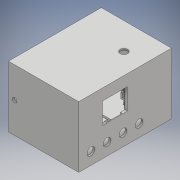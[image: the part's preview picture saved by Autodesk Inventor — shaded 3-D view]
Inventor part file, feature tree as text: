
AUTODESK INVENTOR PART (.ipt)
format: ipt  version: 2018 (Build 220112000, 112)  size: 893,952 bytes
history: native  units: mm
features: sketch x52, extrude x51, other x7
ambient origin geometry x8: Origin, YZ Plane, XZ Plane, XY Plane, X Axis, Y Axis, Z Axis, Center Point
bodies: Body1 (feature_tree)
feature tree (110):
  other  "Sólido1"
  extrude  "Extrusão1"  Depth=156.0mm
  extrude  "Extrusão2"  Depth=3.0mm
  extrude  "Extrusão3"  Depth=3.0mm
  extrude  "Extrusão4"  Depth=100.0mm TaperAngle=0.0deg
  extrude  "Extrusão6"  Depth=5.0mm
  extrude  "Extrusão8"  Depth=5.0mm
  extrude  "Extrusão9"  Depth=70.0mm
  other  "Plano de trabalho3"
  extrude  "Extrusão14"  Depth=7.0mm TaperAngle=0.0deg
  sketch  "Esboço32"  dims[d50=12.0mm d52=12.0mm]
  other  "Plano de trabalho4"
  extrude  "Extrusão15"  Depth=12.0mm
  extrude  "Extrusão16"  Depth=12.0mm
  other  "Plano de trabalho8"
  other  "Plano de trabalho9"
  extrude  "Extrusão19"  Depth=27.0mm
  extrude  "Extrusão20"  Depth=27.0mm
  extrude  "Extrusão21"  Depth=40.5mm
  extrude  "Extrusão22"  Depth=28.5mm
  other  "Plano de trabalho10"
  extrude  "Extrusão27"  Depth=28.5mm
  extrude  "Extrusão28"  Depth=20.5mm
  extrude  "Extrusão31"  Depth=20.25mm TaperAngle=0.0deg
  extrude  "Extrusão32"  Depth=5.25mm
  extrude  "Extrusão33"  Depth=52.0mm
  extrude  "Extrusão34"  Depth=3.0mm
  extrude  "Extrusão35"  Depth=3.0mm
  other  "Plano de trabalho11"
  extrude  "Extrusão36"  Depth=1.25mm
  extrude  "Extrusão37"  Depth=5.25mm
  extrude  "Extrusão38"  Depth=1.0mm
  extrude  "Extrusão39"  Depth=7.0mm
  extrude  "Extrusão40"  Depth=1.0mm
  extrude  "Extrusão41"  Depth=5.0mm
  extrude  "Extrusão42"  Depth=3.0mm TaperAngle=0.0deg
  extrude  "Extrusão43"  Depth=51.5mm
  extrude  "Extrusão44"  Depth=35.0mm
  extrude  "Extrusão47"  Depth=51.5mm TaperAngle=0.0deg
  extrude  "Extrusão48"  Depth=3.0mm
  extrude  "Extrusão49"  Depth=3.0mm
  extrude  "Extrusão50"  Depth=51.5mm TaperAngle=0.0deg
  extrude  "Extrusão51"  [1 undecoded]
  extrude  "Extrusão52"  Depth=3.0mm
  extrude  "Extrusão56"  Depth=3.0mm
  extrude  "Extrusão57"  Depth=20.0mm
  extrude  "Extrusão58"  Depth=20.0mm
  extrude  "Extrusão59"  Depth=25.0mm
  extrude  "Extrusão60"  Depth=28.0mm
  extrude  "Extrusão61"  Depth=3.0mm
  extrude  "Extrusão62"  Depth=11.9mm
  extrude  "Extrusão63"  Depth=35.0mm
  extrude  "Extrusão64"  Depth=3.0mm TaperAngle=0.0deg
  extrude  "Extrusão65"  Depth=97.0mm
  extrude  "Extrusão66"  Depth=1.25mm
  extrude  "Extrusão67"  Depth=2.0mm
  extrude  "Extrusão68"  Depth=2.0mm
  extrude  "Extrusão69"  Depth=59.5mm
  extrude  "Extrusão70"  Depth=10.0mm TaperAngle=0.0deg
  sketch  "Esboço1"  dims[d0=118.0mm d1=156.0mm]
  sketch  "Esboço2"  dims[d2=3.0mm d3=0.0mm d4=3.0mm]
  sketch  "Esboço3"  dims[d5=3.0mm d6=3.0mm]
  sketch  "Esboço4"  dims[d7=3.0mm d8=100.0mm d9=0.0mm]
  sketch  "Esboço6"  dims[d12=5.0mm d13=5.0mm]
  sketch  "Esboço5"  dims[d10=5.0mm d11=5.0mm]
  sketch  "Esboço15"  dims[d14=95.0mm d15=70.0mm]
  sketch  "Esboço17"  dims[d16=5.0mm d17=0.0mm d20=7.0mm d21=0.0mm]
  sketch  "Esboço30"  dims[d46=2.1mm d47=0.0mm d48=12.0mm]
  sketch  "Esboço34"  dims[d54=12.0mm d58=27.0mm]
  sketch  "Esboço45"  dims[d59=27.0mm d60=27.0mm]
  sketch  "Esboço46"  dims[d61=40.5mm d62=34.5mm]
  sketch  "Esboço48"  dims[d68=20.5mm d72=28.5mm]
  sketch  "Esboço49"  dims[d73=28.5mm d74=28.5mm]
  sketch  "Esboço61"  dims[d75=28.5mm d76=20.5mm]
  sketch  "Esboço62"  dims[d77=20.25mm d78=20.0mm d79=0.0mm]
  sketch  "Esboço67"  dims[d82=1.25mm d83=5.25mm]
  sketch  "Esboço68"  dims[d84=49.0mm d85=52.0mm]
  sketch  "Esboço76"  dims[d88=3.0mm d89=3.0mm]
  sketch  "Esboço77"  dims[d90=3.0mm d91=3.0mm]
  sketch  "Esboço80"  dims[d98=1.25mm d99=1.25mm]
  sketch  "Esboço82"  dims[d100=6.25mm d101=5.25mm]
  sketch  "Esboço84"  dims[d102=1.0mm d103=0.0mm d108=1.0mm]
  sketch  "Esboço85"  dims[d109=1.0mm d110=7.0mm]
  sketch  "Esboço86"  dims[d111=7.0mm d112=1.0mm]
  sketch  "Esboço89"  dims[d113=1.0mm d114=5.0mm]
  sketch  "Esboço90"  dims[d115=22.0mm d116=3.0mm d117=0.0mm]
  sketch  "Esboço98"  dims[d167=-1.745329mm d168=51.5mm]
  sketch  "Esboço99"  dims[d169=43.5mm d170=35.0mm]
  sketch  "Esboço101"  dims[d171=10.0mm d172=51.5mm d173=0.0mm]
  sketch  "Esboço102"  dims[d174=3.0mm d175=3.0mm]
  sketch  "Esboço103"  dims[d176=3.0mm d177=3.0mm]
  sketch  "Esboço104"  dims[d178=-1.0mm d179=51.5mm d180=0.0mm]
  sketch  "Esboço105"  dims[d181=2.0mm d182=0.0mm d191=-1.745329mm d192=-2.0mm]
  sketch  "Esboço107"  dims[d197=3.0mm d198=3.0mm]
  sketch  "Esboço108"  dims[d199=3.0mm d200=3.0mm]
  sketch  "Esboço114"  dims[d201=20.0mm d202=20.0mm]
  sketch  "Esboço115"  dims[d203=20.0mm d204=20.0mm]
  sketch  "Esboço116"  dims[d205=20.1mm d206=25.0mm]
  sketch  "Esboço117"  dims[d207=28.0mm d210=2.5mm]
  sketch  "Esboço119"  dims[d211=10.0mm d212=0.0mm d213=3.0mm]
  sketch  "Esboço120"  dims[d214=10.0mm d215=0.0mm d216=11.9mm]
  sketch  "Esboço121"  dims[d217=45.0mm d218=35.0mm]
  sketch  "Esboço122"  dims[d219=10.0mm d220=0.0mm d222=3.0mm d223=0.0mm]
  sketch  "Esboço124"  dims[d227=90.0mm d228=97.0mm]
  sketch  "Esboço125"  dims[d263=2.5mm d264=1.25mm]
  sketch  "Esboço127"  dims[d266=1.745329mm d267=2.0mm]
  sketch  "Esboço128"  dims[d268=2.0mm d269=0.0mm d274=8.0mm]
  sketch  "Esboço129"  dims[d275=3.0mm d280=59.5mm]
  sketch  "Esboço130"  dims[d281=55.0mm d282=10.0mm d283=0.0mm]
  sketch  "Esboço131"  dims[d310=3.0mm d311=3.0mm d312=5.0mm d313=5.0mm d314=20.0mm d315=20.0mm d316=10.0mm d317=0.0mm d318=3.0mm d319=3.0mm d320=3.0mm d321=3.0mm d322=3.0mm d323=0.0mm d330=1.0mm d331=0.0mm d332=7.1mm d333=51.5mm d334=10.5mm d335=10.0mm d336=0.0mm d340=2.0mm d341=4.0mm d342=7.0mm d343=10.0mm d344=0.0mm d345=1.745329mm d346=43.5mm d347=51.5mm d348=3.0mm d349=3.0mm d350=3.0mm d351=3.0mm d352=12.2mm d353=0.0mm d354=1.0mm d355=0.0mm d356=6.0mm d357=3.0mm d358=3.0mm d359=10.0mm d360=20.0mm d361=3.0mm d362=0.0mm d363=20.0mm d364=10.0mm d365=6.0mm d366=3.0mm d367=3.0mm d368=3.0mm d369=0.0mm d370=6.0mm d371=3.0mm d372=15.0mm d373=10.0mm d374=3.0mm d375=3.0mm d376=0.0mm d377=15.0mm d378=10.0mm d379=3.0mm d380=6.0mm d381=3.0mm d382=3.0mm d383=0.0mm d385=22.0mm d386=32.5mm d387=5.0mm d388=48.0mm d390=3.5mm d391=9.5mm d392=9.5mm d393=4.5mm d394=4.5mm d399=10.0mm d400=0.0mm d401=3.5mm d415=22.0mm d416=32.5mm d417=5.0mm d418=48.0mm d419=11.0mm d421=16.5mm d423=4.0mm d424=17.0mm d425=2.0mm d426=0.0mm d427=7.5mm d428=10.0mm d429=0.0mm d430=0.5mm d431=0.5mm d432=0.5mm d433=0.5mm d442=10.0mm d443=0.0mm d444=0.5mm d445=0.5mm d446=0.5mm d447=0.5mm d448=10.0mm d449=0.0mm d450=0.5mm d451=10.0mm d452=0.0mm d453=13.0mm d454=13.0mm d455=13.0mm d456=13.0mm d457=10.0mm d458=0.0mm d459=12.9mm d460=10.0mm d461=0.0mm d462=0.1mm d463=0.1mm d464=0.1mm d465=0.1mm d466=0.1mm d467=0.1mm d468=0.1mm d469=0.1mm d470=0.1mm d471=0.1mm d472=0.1mm d473=0.1mm d474=0.1mm d475=0.1mm d476=10.0mm d477=0.0mm d495=10.0mm d496=0.0mm d497=0.5mm d498=0.5mm d499=0.5mm d500=0.5mm d501=10.0mm d502=0.0mm d503=0.5mm d504=0.5mm d505=0.5mm d506=0.5mm d507=10.0mm d508=0.0mm d509=10.0mm d510=0.0mm d515=0.5mm d516=0.5mm d517=0.5mm d518=0.5mm d519=3.0mm d520=0.0mm d521=0.5mm d522=0.0mm d523=0.5mm d524=0.0mm d525=0.5mm d526=0.5mm d527=10.0mm d528=0.0mm d529=0.5mm d530=0.5mm d531=0.5mm d532=0.5mm d533=10.0mm d534=0.0mm d535=0.5mm d536=0.5mm d537=0.5mm d538=0.5mm d539=10.0mm d540=0.0mm d541=2.0mm d542=10.0mm d543=0.0mm d544=10.0mm d545=0.0mm d546=0.5mm d547=52.0mm d548=0.0mm d549=0.0mm d550=10.0mm d551=0.0mm d552=20.6mm d553=3.0mm d554=1.5mm d555=2.5mm d556=20.0mm d557=20.0mm d558=3.0mm d559=0.0mm]
note: 1 required parameter value undecoded (feature->parameter linkage not recoverable at this tier; creation-order binding heuristic only, values carry confidence <= 0.55)
